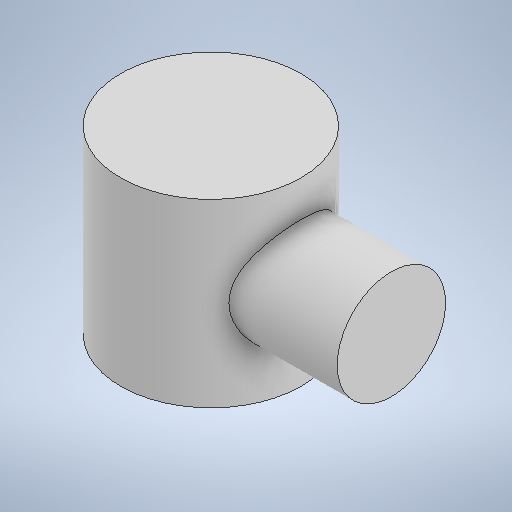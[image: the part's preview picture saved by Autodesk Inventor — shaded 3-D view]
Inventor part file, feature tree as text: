
AUTODESK INVENTOR PART (.ipt)
format: ipt  version: 2025.1 (Build 291241000, 241)  size: 240,128 bytes
history: native  units: mm
features: sketch x3, extrude x2, hole x1, plane x1
ambient origin geometry x8: Origin, YZ Plane, XZ Plane, XY Plane, X Axis, Y Axis, Z Axis, Center Point
bodies: Solid1 (feature_tree)
feature tree (7):
  extrude  "Extrusion1"  Depth=10.0mm TaperAngle=0.0deg
  hole  "Hole1"  [1 undecoded]
  plane  "Work Plane1"
  extrude  "Extrusion2"  Depth=10.0mm TaperAngle=0.0deg
  sketch  "Sketch1"  dims[d0=10.0mm d1=10.0mm d2=0.0mm]
  sketch  "Sketch2"  dims[d3=6.0mm d4=6.0mm d5=4.0mm d6=2.0mm d7=90.0deg d8=8.0mm d9=0.0mm d10=10.0mm]
  sketch  "Sketch3"  dims[d11=6.0mm d12=10.0mm d13=0.0mm]
note: 1 required parameter value undecoded (feature->parameter linkage not recoverable at this tier; creation-order binding heuristic only, values carry confidence <= 0.55)
